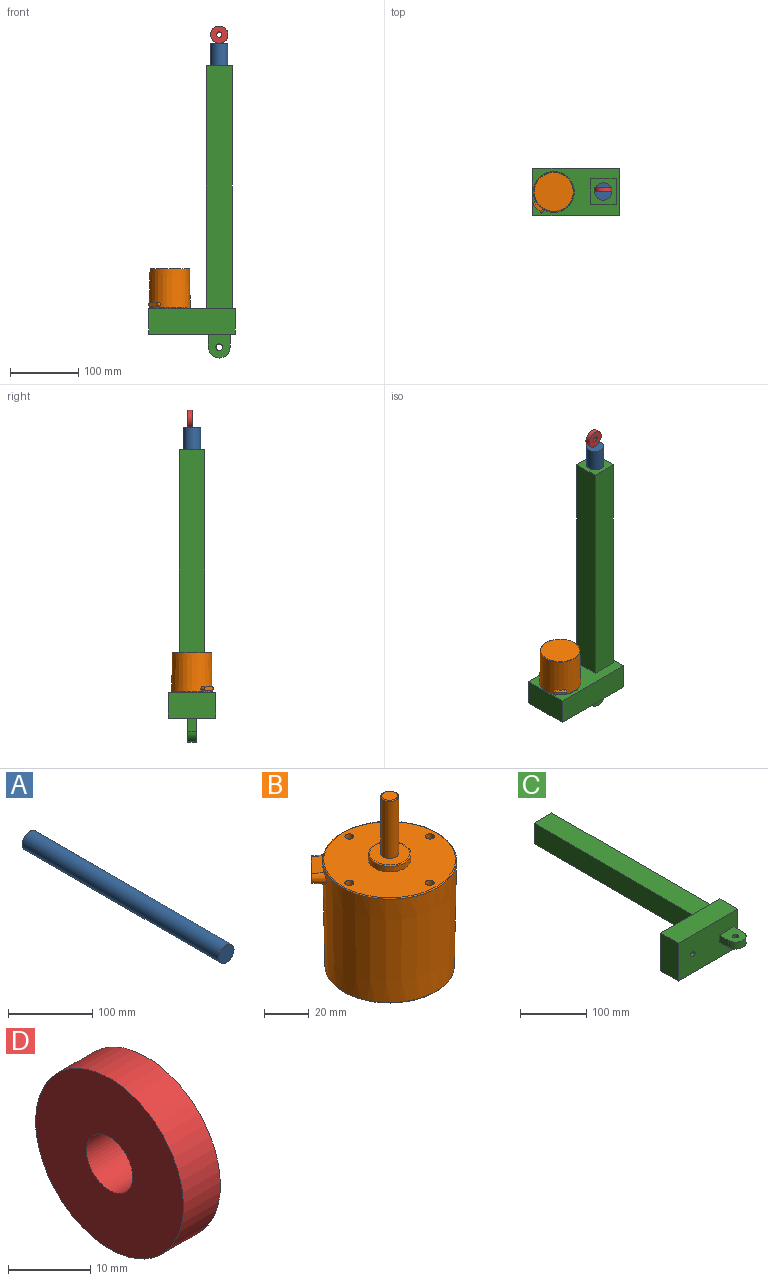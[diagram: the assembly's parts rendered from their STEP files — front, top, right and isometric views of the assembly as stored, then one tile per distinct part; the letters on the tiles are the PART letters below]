
ASSEMBLY  parts=4 mates=3
PART A: 3 faces, bbox 25.4x330.2x25.4 mm
  f0: cylinder r=12.7mm len=330.2mm, axis (0,1,0), area 26348.8mm2, adj f1,f2
  f1: plane 25.4x25.4mm, normal (0,-1,0), area 506.7mm2, adj f0
  f2: plane 25.4x25.4mm, normal (0,1,0), area 506.7mm2, adj f0
PART B: 29 faces, bbox 65.1x65.1x93.4 mm
  f0: torus R=9.03mm, axis (0,0,1), area 46.1mm2, adj f1,f2
  f1: cylinder r=9.53mm len=19.05mm, axis (0,0,-1), area 179.5mm2, adj f0,f3
  f2: plane 18.05x18.05mm, normal (0,0,1), area 205.6mm2, adj f0,f4
  f3: plane 58.98x58.98mm, normal (0,0,1), area 2396.1mm2, adj f1,f5,f6,f7,f8,f9
  f4: cylinder r=4mm len=31mm, axis (0,0,-1), area 732mm2, adj f2,f10,f11,f12,f13,f14
  f5: cylinder r=2.02mm len=5.5mm, axis (0,0,1), area 69.8mm2, adj f3,f15
  f6: cylinder r=2.02mm len=5.5mm, axis (0,0,1), area 69.8mm2, adj f3,f16
  f7: cylinder r=2.02mm len=5.5mm, axis (0,0,1), area 69.8mm2, adj f3,f17
  f8: cylinder r=2.02mm len=5.5mm, axis (0,0,1), area 69.8mm2, adj f3,f18
  f9: torus R=29.49mm, axis (0,0,1), area 148.7mm2, adj f3,f19
  f10: cylinder r=1mm len=2mm, axis (0,1,0), area 3.4mm2, adj f4,f11,f13,f20
  f11: plane 22x1.02mm, normal (-1,0,0), area 22.5mm2, adj f4,f10,f12,f20
  f12: cylinder r=1mm len=2mm, axis (0,1,0), area 3.2mm2, adj f4,f11,f13,f20
  f13: plane 22x1.02mm, normal (1,0,0), area 22.5mm2, adj f4,f10,f12,f20
  f14: torus R=3.5mm, axis (0,0,1), area 18.8mm2, adj f4,f21
  f15: cone r=2.02mm half-angle=59deg, axis (0,0,1), area 14.9mm2, adj f5
  f16: cone r=2.02mm half-angle=59deg, axis (0,0,1), area 14.9mm2, adj f6
  f17: cone r=2.02mm half-angle=59deg, axis (0,0,1), area 14.9mm2, adj f7
  f18: cone r=2.02mm half-angle=59deg, axis (0,0,1), area 14.9mm2, adj f8
  f19: cone r=30mm half-angle=1deg, axis (0,0,1), area 10505mm2, adj f9,f22,f23,f24,f25,f26
  f20: plane 24x2mm, normal (0,1,0), area 47.1mm2, adj f10,f11,f12,f13
  f21: plane 7x7mm, normal (0,0,1), area 38.5mm2, adj f14
  f22: cone r=2.8mm half-angle=5deg, axis (0.71,-0.71,0.02), area 51.9mm2, adj f19,f23,f25,f28
  f23: plane 13.69x13.64mm, normal (-0.06,0.04,-1), area 70.7mm2, adj f19,f22,f24,f28
  f24: cone r=2.8mm half-angle=5deg, axis (0.71,-0.71,0.02), area 51.5mm2, adj f19,f23,f25,f28
  f25: plane 13.7x13.69mm, normal (-0.06,0.09,0.99), area 70.6mm2, adj f19,f22,f24,f28
  f26: torus R=28.49mm, axis (0,0,1), area 140.6mm2, adj f19,f27
  f27: plane 56.98x56.98mm, normal (0,0,-1), area 2550.3mm2, adj f26
  f28: plane 12.82x12.81mm, normal (-0.71,0.71,-0.02), area 80.9mm2, adj f22,f23,f24,f25
PART C: 20 faces, bbox 127x428.6x69.9 mm
  f0: plane 355.6x38.1mm, normal (1,0,0), area 13548.4mm2, adj f1,f3,f5,f7
  f1: plane 355.6x38.1mm, normal (0,0,1), area 13548.4mm2, adj f0,f2,f5,f7
  f2: plane 355.6x38.1mm, normal (-1,0,0), area 13548.4mm2, adj f1,f3,f5,f7
  f3: plane 355.6x38.1mm, normal (0,0,-1), area 13548.4mm2, adj f0,f2,f5,f7
  f4: cylinder r=12.7mm len=355.6mm, axis (0,1,0), area 28375.6mm2, adj f5,f6
  f5: plane 38.1x38.1mm, normal (0,1,0), area 944.9mm2, adj f0,f1,f2,f3,f4
  f6: plane 25.4x25.4mm, normal (0,1,0), area 506.7mm2, adj f4
  f7: plane 127x69.85mm, normal (0,1,0), area 7348.1mm2, adj f0,f1,f2,f3,f8,f9,f10,f11
  f8: plane 127x38.1mm, normal (0,0,1), area 4838.7mm2, adj f7,f9,f11,f12
  f9: plane 69.85x38.1mm, normal (-1,0,0), area 2661.3mm2, adj f7,f8,f10,f12
  f10: plane 127x38.1mm, normal (0,0,-1), area 4838.7mm2, adj f7,f9,f11,f12
  f11: plane 69.85x38.1mm, normal (1,0,0), area 2661.3mm2, adj f7,f8,f10,f12
  f12: plane 127x69.85mm, normal (0,-1,0), area 8396.5mm2, adj f8,f9,f10,f11,f13,f16,f17,f18
  f13: plane 19.05x12.7mm, normal (-1,0,0), area 241.9mm2, adj f12,f14,f17,f18
  f14: cylinder r=15.88mm len=31.75mm, axis (0,0,-1), area 633.4mm2, adj f13,f16,f17,f18
  f15: cylinder r=4.76mm len=12.7mm, axis (0,0,-1), area 380mm2, adj f17,f18
  f16: plane 19.05x12.7mm, normal (1,0,0), area 241.9mm2, adj f12,f14,f17,f18
  f17: plane 34.93x31.75mm, normal (0,0,1), area 929.4mm2, adj f12,f13,f14,f15,f16
  f18: plane 34.93x31.75mm, normal (0,0,-1), area 929.4mm2, adj f12,f13,f14,f15,f16
  f19: cylinder r=4.76mm len=38.1mm, axis (0,1,0), area 1140.1mm2, adj f7,f12
PART D: 4 faces, bbox 6.4x25.4x25.4 mm
  f0: cylinder r=3.97mm len=7.94mm, axis (-1,0,0), area 158.3mm2, adj f2,f3
  f1: cylinder r=12.7mm len=25.4mm, axis (-1,0,0), area 506.7mm2, adj f2,f3
  f2: plane 25.4x25.4mm, normal (1,0,0), area 457.2mm2, adj f0,f1
  f3: plane 25.4x25.4mm, normal (-1,0,0), area 457.2mm2, adj f0,f1
PLACE A rot(axis=(0,0.71,-0.71),180deg) t=(47.21,0,223.47)mm
PLACE B rot(axis=(1,0,0),180deg) t=(-25.32,0,0)mm
PLACE C rot(axis=(1,0,0),90deg) t=(47.21,0,177.8)mm
PLACE D rot(axis=(-0.7,0.7,-0.12),166deg) t=(-120.07,3.18,341.02)mm
MATE planar D.f1 <-> C.f14  axis (0,1,0) through (47.21,6.35,401.27)mm
MATE fastened B.f0 <-> C.f19  axis (0,0,-1) through (-25.32,0,0)mm
MATE cylindrical A.f0 <-> C.f4  axis (0,0,-1) through (47.21,0,58.37)mm
